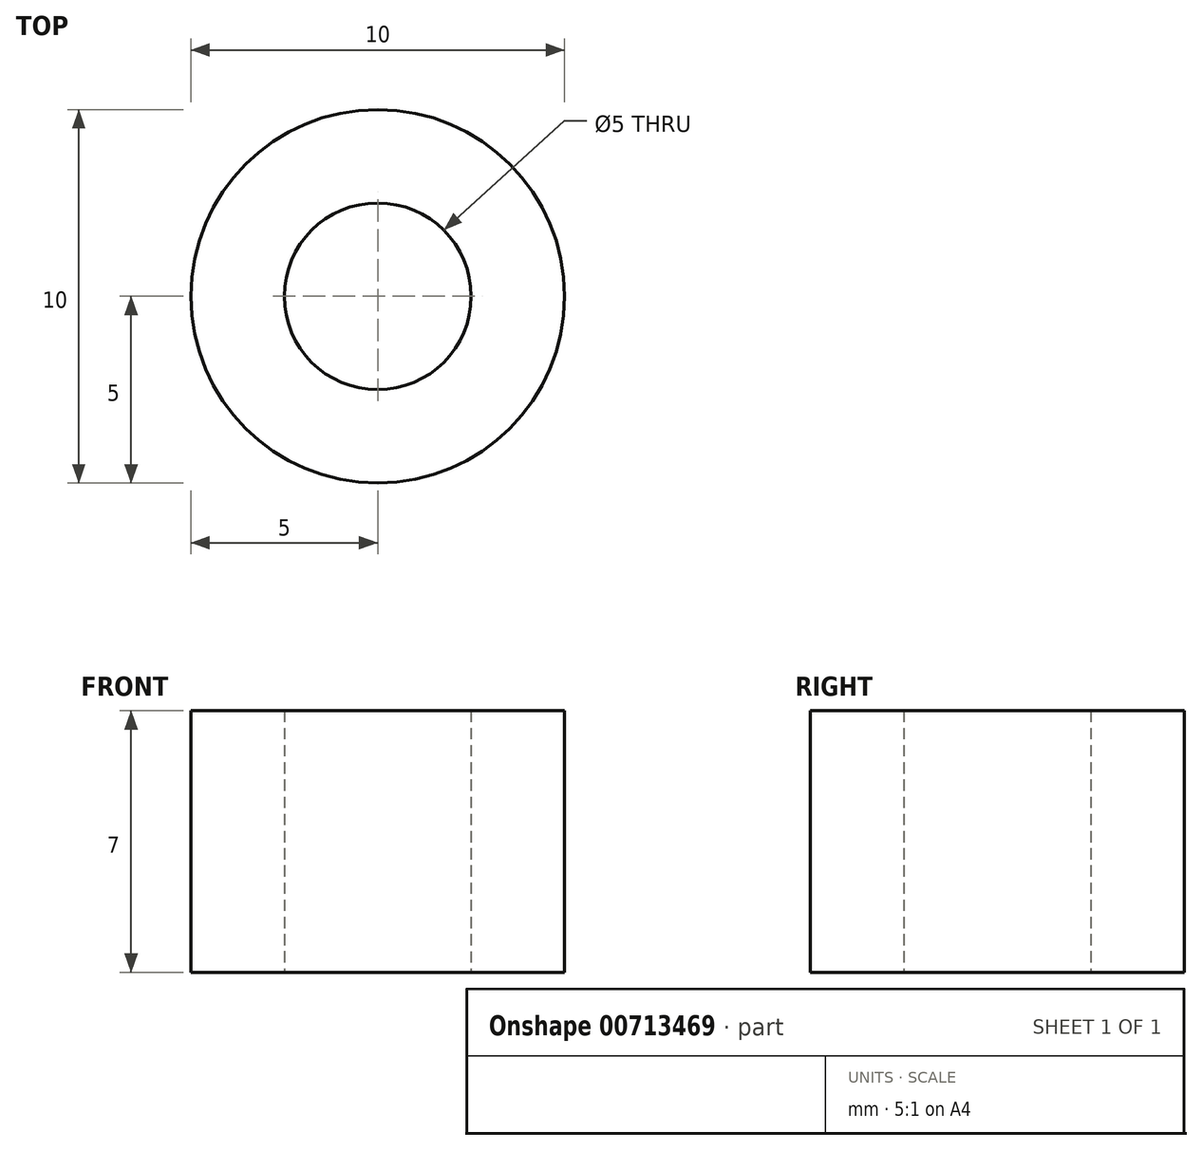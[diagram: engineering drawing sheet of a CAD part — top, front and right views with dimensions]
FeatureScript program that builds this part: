
annotation { "Feature Type Name" : "Feature", "Feature Type Description" : "" }
export const myFeature = defineFeature(function(context is Context, id is Id, definition is map)
    precondition{}
    {
        {
            assignVariable(context, id + "F0", {"name" : "length", "anyValue" : 7 * mm});
        }
        {
            var Q0;
            Q0=qCreatedBy(makeId("Top.planeOp"),FACE);
            var sketch = newSketch(context, id + "F1", { "sketchPlane" : qUnion([Q0])});
            skCircle(sketch, "E0", {"center": v(0, 0) * mm, "radius": 2.5 * mm});
            skCircle(sketch, "E1", {"center": v(0, 0) * mm, "radius": 5 * mm});
            skSolve(sketch);
        }
        {
            var Q0;
            Q0 = qSketchRegion(id + "F1", true);
            extrude(context, id + "F2", {"entities" : qUnion([Q0]), "depth" : getVariable(context, 'length'), "offsetDistance" : 25 * mm});
        }
    });
